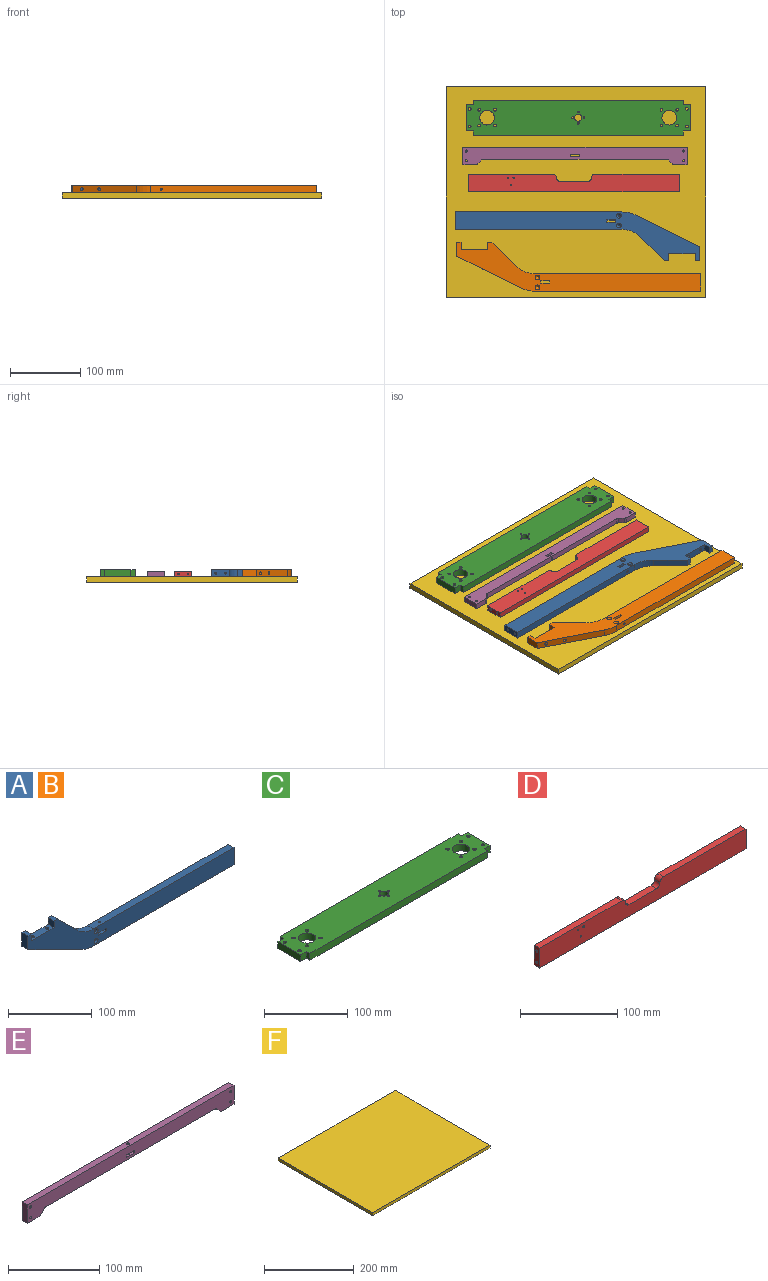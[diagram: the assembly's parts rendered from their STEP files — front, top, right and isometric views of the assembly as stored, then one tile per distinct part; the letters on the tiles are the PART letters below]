
ASSEMBLY  parts=6 mates=5
PART A: 31 faces, bbox 348.4x10.4x70.4 mm
  f0: plane 10x3.5mm, normal (-1,0,0), area 35mm2, adj f1,f16,f17,f18
  f1: plane 12.5x10mm, normal (0,0,1), area 117.9mm2, adj f0,f2,f17,f18,f26
  f2: plane 10x3.5mm, normal (1,0,0), area 35mm2, adj f1,f16,f17,f18
  f3: plane 237.26x10mm, normal (0,0,1), area 2365.5mm2, adj f4,f15,f17,f18,f25
  f4: cylinder r=38mm len=26.87mm, axis (0,1,0), area 298.5mm2, adj f3,f5,f17,f18
  f5: plane 33.87x33.87mm, normal (0.71,0,0.71), area 479mm2, adj f4,f6,f17,f18
  f6: plane 10x5.8mm, normal (0,0,1), area 58mm2, adj f5,f7,f17,f18
  f7: plane 10x10mm, normal (-1,0,0), area 100mm2, adj f6,f8,f17,f18
  f8: plane 38.4x10mm, normal (0,0,1), area 358.9mm2, adj f7,f9,f17,f18,f19,f20
  f9: plane 10x10mm, normal (1,0,0), area 100mm2, adj f8,f10,f17,f18
  f10: plane 10x5.8mm, normal (0,0,1), area 58mm2, adj f9,f11,f17,f18
  f11: plane 20x10mm, normal (-1,0,0), area 200mm2, adj f10,f12,f17,f18
  f12: plane 90.81x45.62mm, normal (-0.45,0,-0.89), area 982.5mm2, adj f11,f13,f17,f18,f19,f20
  f13: cylinder r=45.5mm len=20.35mm, axis (0,1,0), area 210.9mm2, adj f12,f14,f17,f18
  f14: plane 237.26x10mm, normal (0,0,-1), area 2365.5mm2, adj f13,f15,f17,f18,f26
  f15: plane 25x10mm, normal (1,0,0), area 240.2mm2, adj f3,f14,f17,f18,f22,f24
  f16: plane 12.5x10mm, normal (0,0,-1), area 117.9mm2, adj f0,f2,f17,f18,f25
  f17: plane 348x70mm, normal (0,-1,0), area 8986.1mm2, adj f0,f1,f2,f3,f4,f5,f6,f7
  f18: plane 348x70mm, normal (0,1,0), area 9047.2mm2, adj f0,f1,f2,f3,f4,f5,f6,f7
  f19: cylinder r=2mm len=29.75mm, axis (0,0,1), area 361.3mm2, adj f8,f12
  f20: cylinder r=2mm len=17.25mm, axis (0,0,1), area 204.2mm2, adj f8,f12
  f21: cone r=0mm half-angle=59deg, axis (1,0,0), area 5.7mm2, adj f22
  f22: cylinder r=1.25mm len=15mm, axis (1,0,0), area 117.8mm2, adj f15,f21
  f23: cone r=0mm half-angle=59deg, axis (1,0,0), area 5.7mm2, adj f24
  f24: cylinder r=1.25mm len=15mm, axis (1,0,0), area 117.8mm2, adj f15,f23
  f25: cylinder r=1.5mm len=10mm, axis (0,0,1), area 94.2mm2, adj f3,f16
  f26: cylinder r=1.5mm len=11.5mm, axis (0,0,1), area 108.4mm2, adj f1,f14
  f27: cylinder r=1.25mm len=7.89mm, axis (0,-1,0), area 62mm2, adj f18,f28
  f28: cone r=1.25mm half-angle=45deg, axis (0,-1,0), area 43.2mm2, adj f17,f27
  f29: cylinder r=1.25mm len=7.89mm, axis (0,-1,0), area 62mm2, adj f18,f30
  f30: cone r=1.25mm half-angle=45deg, axis (0,-1,0), area 43.2mm2, adj f17,f29
PART B: same geometry as A
PART C: 33 faces, bbox 320x50x10 mm
  f0: plane 320x50mm, normal (0,0,1), area 14815.1mm2, adj f2,f3,f4,f5,f6,f7,f8,f9
  f1: plane 320x50mm, normal (0,0,-1), area 14815.1mm2, adj f2,f3,f4,f5,f6,f7,f8,f9
  f2: plane 10x10mm, normal (0,1,0), area 100mm2, adj f0,f1,f3,f23
  f3: plane 38x10mm, normal (-1,0,0), area 380mm2, adj f0,f1,f2,f4
  f4: plane 10x10mm, normal (0,-1,0), area 100mm2, adj f0,f1,f3,f5
  f5: plane 10x6mm, normal (-1,0,0), area 60mm2, adj f0,f1,f4,f6
  f6: plane 300x10mm, normal (0,-1,0), area 3000mm2, adj f0,f1,f5,f7
  f7: plane 10x6mm, normal (1,0,0), area 60mm2, adj f0,f1,f6,f8
  f8: plane 10x10mm, normal (0,-1,0), area 100mm2, adj f0,f1,f7,f9
  f9: plane 38x10mm, normal (1,0,0), area 380mm2, adj f0,f1,f8,f10
  f10: plane 10x10mm, normal (0,1,0), area 100mm2, adj f0,f1,f9,f11
  f11: plane 10x6mm, normal (1,0,0), area 60mm2, adj f0,f1,f10,f12
  f12: plane 300x10mm, normal (0,1,0), area 3000mm2, adj f0,f1,f11,f23
  f13: cylinder r=10.5mm len=21mm, axis (0,0,-1), area 659.7mm2, adj f0,f1
  f14: cylinder r=2mm len=10mm, axis (0,0,-1), area 125.7mm2, adj f0,f1
  f15: cylinder r=2mm len=10mm, axis (0,0,-1), area 125.7mm2, adj f0,f1
  f16: cylinder r=2mm len=10mm, axis (0,0,-1), area 125.7mm2, adj f0,f1
  f17: cylinder r=2mm len=10mm, axis (0,0,-1), area 125.7mm2, adj f0,f1
  f18: cylinder r=2mm len=10mm, axis (0,0,-1), area 125.7mm2, adj f0,f1
  f19: cylinder r=2mm len=10mm, axis (0,0,-1), area 125.7mm2, adj f0,f1
  f20: cylinder r=10.5mm len=21mm, axis (0,0,-1), area 659.7mm2, adj f0,f1
  f21: cylinder r=2mm len=10mm, axis (0,0,-1), area 125.7mm2, adj f0,f1
  f22: cylinder r=2mm len=10mm, axis (0,0,-1), area 125.7mm2, adj f0,f1
  f23: plane 10x6mm, normal (-1,0,0), area 60mm2, adj f0,f1,f2,f12
  f24: cylinder r=2mm len=10mm, axis (0,0,1), area 125.7mm2, adj f0,f1
  f25: cylinder r=2mm len=10mm, axis (0,0,1), area 125.7mm2, adj f0,f1
  f26: cylinder r=2mm len=10mm, axis (0,0,1), area 125.7mm2, adj f0,f1
  f27: cylinder r=2mm len=10mm, axis (0,0,1), area 125.7mm2, adj f0,f1
  f28: cylinder r=5.1mm len=10.2mm, axis (0,0,1), area 320.4mm2, adj f0,f1
  f29: cylinder r=1.25mm len=10mm, axis (0,0,1), area 78.5mm2, adj f0,f1
  f30: cylinder r=1.25mm len=10mm, axis (0,0,1), area 78.5mm2, adj f0,f1
  f31: cylinder r=1.25mm len=10mm, axis (0,0,1), area 78.5mm2, adj f0,f1
  f32: cylinder r=1.25mm len=10mm, axis (0,0,1), area 78.5mm2, adj f0,f1
PART D: 23 faces, bbox 300x8x25 mm
  f0: plane 120x8mm, normal (0,0,1), area 960mm2, adj f1,f2,f4,f22
  f1: plane 300x25mm, normal (0,-1,0), area 6990.6mm2, adj f0,f3,f4,f5,f6,f15,f16,f17
  f2: plane 300x25mm, normal (0,1,0), area 6990.6mm2, adj f0,f3,f4,f5,f6,f15,f16,f17
  f3: plane 120x8mm, normal (0,0,1), area 960mm2, adj f1,f2,f6,f20
  f4: plane 25x8mm, normal (-1,0,0), area 191mm2, adj f0,f1,f2,f5,f12,f14
  f5: plane 300x8mm, normal (0,0,-1), area 2400mm2, adj f1,f2,f4,f6
  f6: plane 25x8mm, normal (1,0,0), area 191mm2, adj f1,f2,f3,f5,f8,f10
  f7: cone r=0mm half-angle=59deg, axis (1,0,0), area 5.3mm2, adj f8
  f8: cylinder r=1.2mm len=25mm, axis (1,0,0), area 188.5mm2, adj f6,f7
  f9: cone r=0mm half-angle=59deg, axis (1,0,0), area 5.3mm2, adj f10
  f10: cylinder r=1.2mm len=25mm, axis (1,0,0), area 188.5mm2, adj f6,f9
  f11: cone r=0mm half-angle=59deg, axis (-1,0,0), area 5.3mm2, adj f12
  f12: cylinder r=1.2mm len=25mm, axis (-1,0,0), area 188.5mm2, adj f4,f11
  f13: cone r=0mm half-angle=59deg, axis (-1,0,0), area 5.3mm2, adj f14
  f14: cylinder r=1.2mm len=25mm, axis (-1,0,0), area 188.5mm2, adj f4,f13
  f15: cylinder r=1mm len=8mm, axis (0,-1,0), area 50.3mm2, adj f1,f2
  f16: cylinder r=1mm len=8mm, axis (0,-1,0), area 50.3mm2, adj f1,f2
  f17: cylinder r=1mm len=8mm, axis (0,-1,0), area 50.3mm2, adj f1,f2
  f18: plane 40x8mm, normal (0,0,1), area 320mm2, adj f1,f2,f19,f21
  f19: cylinder r=5mm len=8mm, axis (0,-1,0), area 62.8mm2, adj f1,f2,f18,f20
  f20: cylinder r=5mm len=8mm, axis (0,-1,0), area 62.8mm2, adj f1,f2,f3,f19
  f21: cylinder r=5mm len=8mm, axis (0,1,0), area 62.8mm2, adj f1,f2,f18,f22
  f22: cylinder r=5mm len=8mm, axis (0,1,0), area 62.8mm2, adj f0,f1,f2,f21
PART E: 24 faces, bbox 320x8x25 mm
  f0: plane 8x5.66mm, normal (-0.71,0,-0.71), area 64mm2, adj f16,f17,f20,f23
  f1: plane 18.34x8mm, normal (0,0,-1), area 146.7mm2, adj f2,f16,f17,f20
  f2: plane 25x8mm, normal (1,0,0), area 200mm2, adj f1,f3,f16,f17
  f3: plane 320x8mm, normal (0,0,1), area 2552.9mm2, adj f2,f4,f16,f17,f19
  f4: plane 25x8mm, normal (-1,0,0), area 200mm2, adj f3,f5,f16,f17
  f5: plane 18.34x8mm, normal (0,0,-1), area 146.7mm2, adj f4,f16,f17,f21
  f6: plane 8x5.66mm, normal (0.71,0,-0.71), area 64mm2, adj f16,f17,f21,f22
  f7: plane 8x3.5mm, normal (1,0,0), area 28mm2, adj f8,f14,f16,f17
  f8: plane 12.5x8mm, normal (0,0,-1), area 92.9mm2, adj f7,f9,f16,f17,f19
  f9: plane 8x3.5mm, normal (-1,0,0), area 28mm2, adj f8,f14,f16,f17
  f10: cylinder r=1.5mm len=8mm, axis (0,1,0), area 75.4mm2, adj f16,f17
  f11: cylinder r=1.5mm len=8mm, axis (0,1,0), area 75.4mm2, adj f16,f17
  f12: cylinder r=1.5mm len=8mm, axis (0,1,0), area 75.4mm2, adj f16,f17
  f13: cylinder r=1.5mm len=8mm, axis (0,1,0), area 75.4mm2, adj f16,f17
  f14: plane 12.5x8mm, normal (0,0,1), area 92.9mm2, adj f7,f9,f16,f17,f18
  f15: plane 260.69x8mm, normal (0,0,-1), area 2078.4mm2, adj f16,f17,f18,f22,f23
  f16: plane 320x25mm, normal (0,-1,0), area 5752mm2, adj f0,f1,f2,f3,f4,f5,f6,f7
  f17: plane 320x25mm, normal (0,1,0), area 5752mm2, adj f0,f1,f2,f3,f4,f5,f6,f7
  f18: cylinder r=1.5mm len=3.5mm, axis (0,0,1), area 33mm2, adj f14,f15
  f19: cylinder r=1.5mm len=10mm, axis (0,0,1), area 94.2mm2, adj f3,f8
  f20: cylinder r=4mm len=8mm, axis (0,1,0), area 25.1mm2, adj f0,f1,f16,f17
  f21: cylinder r=4mm len=8mm, axis (0,1,0), area 25.1mm2, adj f5,f6,f16,f17
  f22: cylinder r=4mm len=8mm, axis (0,-1,0), area 25.1mm2, adj f6,f15,f16,f17
  f23: cylinder r=4mm len=8mm, axis (0,-1,0), area 25.1mm2, adj f0,f15,f16,f17
PART F: 6 faces, bbox 370x300x8 mm
  f0: plane 370x8mm, normal (0,1,0), area 2960mm2, adj f1,f3,f4,f5
  f1: plane 300x8mm, normal (-1,0,0), area 2400mm2, adj f0,f2,f4,f5
  f2: plane 370x8mm, normal (0,-1,0), area 2960mm2, adj f1,f3,f4,f5
  f3: plane 300x8mm, normal (1,0,0), area 2400mm2, adj f0,f2,f4,f5
  f4: plane 370x300mm, normal (0,0,1), area 111000mm2, adj f0,f1,f2,f3
  f5: plane 370x300mm, normal (0,0,-1), area 111000mm2, adj f0,f1,f2,f3
PLACE A rot(axis=(0,0.71,-0.71),180deg) t=(176.23,-98.47,13)mm
PLACE B rot(axis=(-1,0,0),90deg) t=(-169.9,-71.5,13)mm
PLACE C t=(3.19,106.05,8)mm
PLACE D rot(axis=(-1,0,0),90deg) t=(-2.93,12.72,8)mm
PLACE E rot(axis=(-1,0,0),90deg) t=(-1.44,51.45,8)mm
PLACE F at identity
MATE planar A.f27 <-> F.f4  axis (0,0,-1) through (61.23,-33.97,8)mm
MATE planar B.f27 <-> F.f4  axis (0,0,-1) through (-54.9,-136,8)mm
MATE planar D.f20 <-> F.f4  axis (0,0,-1) through (27.07,20.22,8)mm
MATE planar C.f28 <-> F.f4  axis (0,0,-1) through (3.19,106.05,8)mm
MATE planar E.f12 <-> F.f4  axis (0,0,-1) through (153.56,44.45,8)mm
